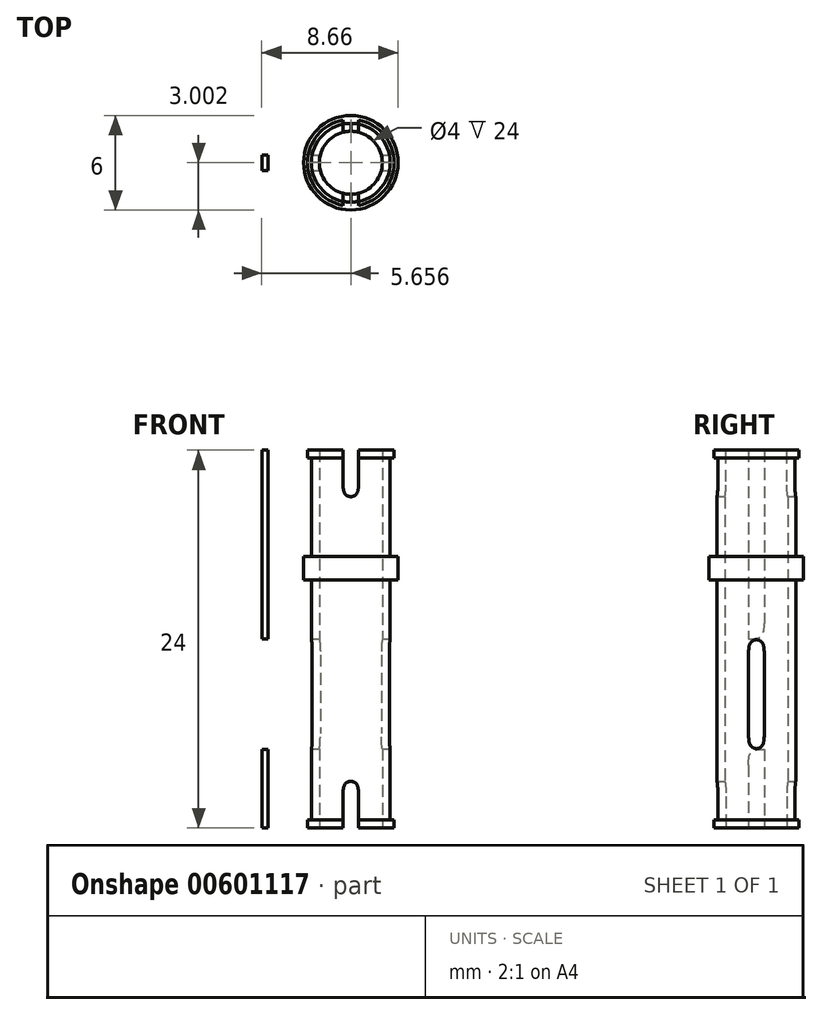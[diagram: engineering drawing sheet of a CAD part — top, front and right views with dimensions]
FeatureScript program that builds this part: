
annotation { "Feature Type Name" : "Feature", "Feature Type Description" : "" }
export const myFeature = defineFeature(function(context is Context, id is Id, definition is map)
    precondition{}
    {
        {
            var Q0;
            Q0=qCreatedBy(makeId("Top.planeOp"),FACE);
            var sketch = newSketch(context, id + "F0", { "sketchPlane" : qUnion([Q0])});
            skCircle(sketch, "E0", {"center": v(-5.92, -30) * mm, "radius": 3 * mm});
            skSolve(sketch);
        }
        {
            var Q0;
            Q0=qSketchRegion(id+"F0",true);
            extrude(context, id + "F1", {"entities" : qUnion([Q0]), "depth" : 24 * mm, "offsetDistance" : 25 * mm});
        }
        {
            var Q0;
            Q0=makeQuery(id+"F1.opExtrude","CAP_FACE",FACE,{"disambiguationData":[OSD([sQuery(id+"F0.wireOp",EDGE,"E0")])],"isStart":false});
            var sketch = newSketch(context, id + "F2", { "sketchPlane" : qUnion([Q0])});
            skCircle(sketch, "E1", {"center": v(-5.92, -30) * mm, "radius": 2.5 * mm});
            skSolve(sketch);
        }
        {
            var Q0;
            Q0=makeQuery(id+"F2.imprint","IMPRINT",FACE,{"disambiguationData":[TD([[makeQuery(id+"F2.imprint","IMPRINT",EDGE,{"derivedFrom":sQuery(id+"F2.wireOp",EDGE,"E1")}),-1.0]])]});
            extrude(context, id + "F3", {"entities" : qUnion([Q0]), "operationType" : NewBodyOperationType.REMOVE, "oppositeDirection" : true, "depth" : 6.75 * mm, "offsetDistance" : 25 * mm});
        }
        {
            var Q0;
            Q0=makeQuery(id+"F1.opExtrude","CAP_FACE",FACE,{"disambiguationData":[OSD([sQuery(id+"F0.wireOp",EDGE,"E0")])],"isStart":false});
            var sketch = newSketch(context, id + "F4", { "sketchPlane" : qUnion([Q0])});
            skCircle(sketch, "E2", {"center": v(-5.92, -30) * mm, "radius": 2.75 * mm});
            skSolve(sketch);
        }
        {
            var Q0;
            Q0=qSketchRegion(id+"F4",true);
            extrude(context, id + "F5", {"entities" : qUnion([Q0]), "operationType" : NewBodyOperationType.ADD, "oppositeDirection" : true, "depth" : .5 * mm, "offsetDistance" : 25 * mm});
        }
        {
            var Q0;
            Q0=makeQuery(id+"F1.opExtrude","CAP_FACE",FACE,{"disambiguationData":[OSD([sQuery(id+"F0.wireOp",EDGE,"E0")])],"isStart":true});
            var sketch = newSketch(context, id + "F6", { "sketchPlane" : qUnion([Q0])});
            skCircle(sketch, "E3", {"center": v(-5.92, 30) * mm, "radius": 2.5 * mm});
            skSolve(sketch);
        }
        {
            var Q0;
            Q0=makeQuery(id+"F6.imprint","IMPRINT",FACE,{"disambiguationData":[TD([[makeQuery(id+"F6.imprint","IMPRINT",EDGE,{"derivedFrom":sQuery(id+"F6.wireOp",EDGE,"E3")}),-1.0]])]});
            extrude(context, id + "F7", {"entities" : qUnion([Q0]), "operationType" : NewBodyOperationType.REMOVE, "oppositeDirection" : true, "depth" : 6.75 * mm, "offsetDistance" : 25 * mm});
        }
        {
            var Q0;
            Q0=makeQuery(id+"F1.opExtrude","CAP_FACE",FACE,{"disambiguationData":[OSD([sQuery(id+"F0.wireOp",EDGE,"E0")])],"isStart":true});
            var sketch = newSketch(context, id + "F8", { "sketchPlane" : qUnion([Q0])});
            skCircle(sketch, "E4", {"center": v(-5.92, 30) * mm, "radius": 2.75 * mm});
            skSolve(sketch);
        }
        {
            var Q0;
            Q0=qSketchRegion(id+"F8",true);
            extrude(context, id + "F9", {"entities" : qUnion([Q0]), "operationType" : NewBodyOperationType.ADD, "oppositeDirection" : true, "depth" : .5 * mm, "offsetDistance" : 25 * mm});
        }
        {
            var Q0;
            Q0=makeQuery(id+"F9.boolean.opBoolean","MERGE",FACE,{"derivedFrom":[makeQuery(id+"F1.opExtrude","CAP_FACE",FACE,{"disambiguationData":[OSD([sQuery(id+"F0.wireOp",EDGE,"E0")])],"isStart":true}),makeQuery(id+"F9.opExtrude","CAP_FACE",FACE,{"disambiguationData":[OSD([sQuery(id+"F8.wireOp",EDGE,"E4")])],"isStart":true})]});
            var sketch = newSketch(context, id + "F10", { "sketchPlane" : qUnion([Q0])});
            skCircle(sketch, "E5", {"center": v(-5.92, 30) * mm, "radius": 2 * mm});
            skSolve(sketch);
        }
        {
            var Q0;
            Q0=qSketchRegion(id+"F10",true);
            extrude(context, id + "F11", {"entities" : qUnion([Q0]), "operationType" : NewBodyOperationType.REMOVE, "oppositeDirection" : true, "depth" : 25 * mm, "offsetDistance" : 25 * mm});
        }
        {
            var Q0;
            Q0=makeQuery(id+"F5.boolean.opBoolean","MERGE",FACE,{"derivedFrom":[makeQuery(id+"F1.opExtrude","CAP_FACE",FACE,{"disambiguationData":[OSD([sQuery(id+"F0.wireOp",EDGE,"E0")])],"isStart":false}),makeQuery(id+"F5.opExtrude","CAP_FACE",FACE,{"disambiguationData":[OSD([sQuery(id+"F4.wireOp",EDGE,"E2")])],"isStart":true})]});
            var sketch = newSketch(context, id + "F12", { "sketchPlane" : qUnion([Q0])});
            skLineSegment(sketch, "E6", {"start": v(-5.92, -33.03) * mm, "end": v(-5.42, -33.03) * mm});
            skLineSegment(sketch, "E7", {"start": v(-5.42, -33.03) * mm, "end": v(-5.42, -27) * mm});
            skLineSegment(sketch, "E8", {"start": v(-5.42, -27) * mm, "end": v(-6.42, -27) * mm});
            skLineSegment(sketch, "E9", {"start": v(-6.42, -27) * mm, "end": v(-6.42, -33.03) * mm});
            skLineSegment(sketch, "E10", {"start": v(-6.42, -33.03) * mm, "end": v(-5.92, -33.03) * mm});
            skSolve(sketch);
        }
        {
            var Q0;
            {var subQ0=sQuery(id+"F12.wireOp",EDGE,"E7");var subQ1=sQuery(id+"F4.wireOp",EDGE,"E2");var subQ2=makeQuery(id+"F5.opExtrude","CAP_EDGE",EDGE,{"disambiguationData":[OSD([subQ1])],"isStart":true});var subQ3=makeQuery(id+"F12.imprint","INTERSECT",VERTEX,{"disambiguationData":[OD(0.0)],"derivedFrom":[subQ2,subQ0]});Q0=makeQuery(id+"F12.imprint","IMPRINT",FACE,{"disambiguationData":[TD([[makeQuery(id+"F12.imprint","IMPRINT",EDGE,{"disambiguationData":[TD([[subQ3,1.0]])],"derivedFrom":subQ2}),1.0]])]});}
            var Q1;
            {var subQ0=sQuery(id+"F12.wireOp",EDGE,"E7");var subQ1=sQuery(id+"F4.wireOp",EDGE,"E2");var subQ2=makeQuery(id+"F5.opExtrude","CAP_EDGE",EDGE,{"disambiguationData":[OSD([subQ1])],"isStart":true});var subQ3=makeQuery(id+"F12.imprint","INTERSECT",VERTEX,{"disambiguationData":[OD(1.0)],"derivedFrom":[subQ2,subQ0]});Q1=makeQuery(id+"F12.imprint","IMPRINT",FACE,{"disambiguationData":[TD([[makeQuery(id+"F12.imprint","IMPRINT",EDGE,{"disambiguationData":[TD([[subQ3,-1.0]])],"derivedFrom":subQ2}),1.0]])]});}
            extrude(context, id + "F13", {"entities" : qUnion([Q0, Q1]), "operationType" : NewBodyOperationType.REMOVE, "oppositeDirection" : true, "depth" : 3 * mm, "offsetDistance" : 25 * mm});
        }
        {
            var Q0;
            Q0=makeQuery(id+"F9.boolean.opBoolean","MERGE",FACE,{"derivedFrom":[makeQuery(id+"F1.opExtrude","CAP_FACE",FACE,{"disambiguationData":[OSD([sQuery(id+"F0.wireOp",EDGE,"E0")])],"isStart":true}),makeQuery(id+"F9.opExtrude","CAP_FACE",FACE,{"disambiguationData":[OSD([sQuery(id+"F8.wireOp",EDGE,"E4")])],"isStart":true})]});
            var sketch = newSketch(context, id + "F14", { "sketchPlane" : qUnion([Q0])});
            skLineSegment(sketch, "E11", {"start": v(-5.92, 33.1) * mm, "end": v(-5.42, 33.1) * mm});
            skLineSegment(sketch, "E12", {"start": v(-5.42, 33.1) * mm, "end": v(-5.42, 26.78) * mm});
            skLineSegment(sketch, "E13", {"start": v(-5.42, 26.78) * mm, "end": v(-6.42, 26.78) * mm});
            skLineSegment(sketch, "E14", {"start": v(-6.42, 26.78) * mm, "end": v(-6.42, 33.1) * mm});
            skLineSegment(sketch, "E15", {"start": v(-6.42, 33.1) * mm, "end": v(-5.92, 33.1) * mm});
            skSolve(sketch);
        }
        {
            var Q0;
            Q0=qSketchRegion(id+"F14",true);
            extrude(context, id + "F15", {"entities" : qUnion([Q0]), "operationType" : NewBodyOperationType.REMOVE, "oppositeDirection" : true, "depth" : 3 * mm, "offsetDistance" : 25 * mm});
        }
        {
            var Q0;
            Q0=makeQuery(id+"F7.boolean.opBoolean","COPY",FACE,{"derivedFrom":makeQuery(id+"F7.opExtrude","CAP_FACE",FACE,{"disambiguationData":[OSD([sQuery(id+"F0.wireOp",EDGE,"E0"),sQuery(id+"F6.wireOp",EDGE,"E3")])],"isStart":false})});
            extrude(context, id + "F16", {"entities" : qUnion([Q0]), "operationType" : NewBodyOperationType.REMOVE, "oppositeDirection" : true, "depth" : 9 * mm, "offsetDistance" : 25 * mm});
        }
        {
            var Q0;
            {var subQ0=sQuery(id+"F12.wireOp",EDGE,"E9");var subQ1=sQuery(id+"F4.wireOp",EDGE,"E2");Q0=makeQuery(id+"F13.boolean.opBoolean","COPY",EDGE,{"derivedFrom":makeQuery(id+"F13.opExtrude","CAP_EDGE",EDGE,{"disambiguationData":[OSD([subQ0]),TDD([makeQuery(id+"F12.imprint","IMPRINT",EDGE,{"disambiguationData":[TD([[makeQuery(id+"F12.imprint","INTERSECT",VERTEX,{"disambiguationData":[OD(1.0)],"derivedFrom":[makeQuery(id+"F5.opExtrude","CAP_EDGE",EDGE,{"disambiguationData":[OSD([subQ1])],"isStart":true}),subQ0]}),1.0]])],"derivedFrom":subQ0})])],"isStart":false})});}
            var Q1;
            {var subQ0=sQuery(id+"F12.wireOp",EDGE,"E7");var subQ1=sQuery(id+"F4.wireOp",EDGE,"E2");Q1=makeQuery(id+"F13.boolean.opBoolean","COPY",EDGE,{"derivedFrom":makeQuery(id+"F13.opExtrude","CAP_EDGE",EDGE,{"disambiguationData":[OSD([subQ0]),TDD([makeQuery(id+"F12.imprint","IMPRINT",EDGE,{"disambiguationData":[TD([[makeQuery(id+"F12.imprint","INTERSECT",VERTEX,{"disambiguationData":[OD(0.0)],"derivedFrom":[makeQuery(id+"F5.opExtrude","CAP_EDGE",EDGE,{"disambiguationData":[OSD([subQ1])],"isStart":true}),subQ0]}),-1.0]])],"derivedFrom":subQ0})])],"isStart":false})});}
            var Q2;
            {var subQ0=sQuery(id+"F12.wireOp",EDGE,"E7");var subQ1=sQuery(id+"F4.wireOp",EDGE,"E2");Q2=makeQuery(id+"F13.boolean.opBoolean","COPY",EDGE,{"derivedFrom":makeQuery(id+"F13.opExtrude","CAP_EDGE",EDGE,{"disambiguationData":[OSD([subQ0]),TDD([makeQuery(id+"F12.imprint","IMPRINT",EDGE,{"disambiguationData":[TD([[makeQuery(id+"F12.imprint","INTERSECT",VERTEX,{"disambiguationData":[OD(1.0)],"derivedFrom":[makeQuery(id+"F5.opExtrude","CAP_EDGE",EDGE,{"disambiguationData":[OSD([subQ1])],"isStart":true}),subQ0]}),1.0]])],"derivedFrom":subQ0})])],"isStart":false})});}
            var Q3;
            {var subQ0=sQuery(id+"F12.wireOp",EDGE,"E9");var subQ1=sQuery(id+"F4.wireOp",EDGE,"E2");Q3=makeQuery(id+"F13.boolean.opBoolean","COPY",EDGE,{"derivedFrom":makeQuery(id+"F13.opExtrude","CAP_EDGE",EDGE,{"disambiguationData":[OSD([subQ0]),TDD([makeQuery(id+"F12.imprint","IMPRINT",EDGE,{"disambiguationData":[TD([[makeQuery(id+"F12.imprint","INTERSECT",VERTEX,{"disambiguationData":[OD(0.0)],"derivedFrom":[makeQuery(id+"F5.opExtrude","CAP_EDGE",EDGE,{"disambiguationData":[OSD([subQ1])],"isStart":true}),subQ0]}),-1.0]])],"derivedFrom":subQ0})])],"isStart":false})});}
            var Q4;
            Q4=makeQuery(id+"F15.boolean.opBoolean","COPY",EDGE,{"disambiguationData":[OD(0.0)],"derivedFrom":makeQuery(id+"F15.opExtrude","CAP_EDGE",EDGE,{"disambiguationData":[OSD([sQuery(id+"F14.wireOp",EDGE,"E12")])],"isStart":false})});
            var Q5;
            Q5=makeQuery(id+"F15.boolean.opBoolean","COPY",EDGE,{"disambiguationData":[OD(0.0)],"derivedFrom":makeQuery(id+"F15.opExtrude","CAP_EDGE",EDGE,{"disambiguationData":[OSD([sQuery(id+"F14.wireOp",EDGE,"E14")])],"isStart":false})});
            var Q6;
            Q6=makeQuery(id+"F15.boolean.opBoolean","COPY",EDGE,{"disambiguationData":[OD(1.0)],"derivedFrom":makeQuery(id+"F15.opExtrude","CAP_EDGE",EDGE,{"disambiguationData":[OSD([sQuery(id+"F14.wireOp",EDGE,"E12")])],"isStart":false})});
            var Q7;
            Q7=makeQuery(id+"F15.boolean.opBoolean","COPY",EDGE,{"disambiguationData":[OD(1.0)],"derivedFrom":makeQuery(id+"F15.opExtrude","CAP_EDGE",EDGE,{"disambiguationData":[OSD([sQuery(id+"F14.wireOp",EDGE,"E14")])],"isStart":false})});
            fillet(context, id + "F17", {"entities" : qUnion([Q0, Q1, Q2, Q3, Q4, Q5, Q6, Q7]), "radius" : 1 * mm, "tangentPropagation" : true, "rho" : .65, "crossSection" : FilletCrossSection.CONIC, "allowEdgeOverflow" : false});
        }
        {
            var Q0;
            {var subQ0=sQuery(id+"F8.wireOp",EDGE,"E4");Q0=makeQuery(id+"F15.boolean.opBoolean","SPLIT",FACE,{"disambiguationData":[TD([makeQuery(id+"F15.opExtrude","SWEPT_FACE",FACE,{"disambiguationData":[OSD([sQuery(id+"F14.wireOp",EDGE,"E14")])]})])],"derivedFrom":makeQuery(id+"F9.boolean.opBoolean","MERGE",FACE,{"derivedFrom":[makeQuery(id+"F1.opExtrude","CAP_FACE",FACE,{"disambiguationData":[OSD([sQuery(id+"F0.wireOp",EDGE,"E0")])],"isStart":true}),makeQuery(id+"F9.opExtrude","CAP_FACE",FACE,{"disambiguationData":[OSD([subQ0])],"isStart":true})]})});}
            var sketch = newSketch(context, id + "F18", { "sketchPlane" : qUnion([Q0])});
            skPoint(sketch, "E16.endSnap0", {"position": v(-8.67, 30) * mm});
            skLineSegment(sketch, "E17", {"start": v(-11.58, 30) * mm, "end": v(-11.58, 29.5) * mm});
            skLineSegment(sketch, "E18", {"start": v(-11.58, 29.5) * mm, "end": v(-11.18, 29.5) * mm});
            skLineSegment(sketch, "E19", {"start": v(-11.18, 29.5) * mm, "end": v(-11.18, 30.5) * mm});
            skLineSegment(sketch, "E20", {"start": v(-11.18, 30.5) * mm, "end": v(-11.58, 30.5) * mm});
            skLineSegment(sketch, "E21", {"start": v(-11.58, 30.5) * mm, "end": v(-11.58, 30) * mm});
            skSolve(sketch);
        }
        {
            var Q0;
            Q0=makeQuery(id+"F18.imprint","IMPRINT",FACE,{"disambiguationData":[TD([[makeQuery(id+"F18.imprint","IMPRINT",EDGE,{"derivedFrom":sQuery(id+"F18.wireOp",EDGE,"E17")}),1.0]])]});
            extrude(context, id + "F19", {"entities" : qUnion([Q0]), "oppositeDirection" : true, "depth" : 24 * mm, "offsetDistance" : 25 * mm});
        }
        {
            var Q0;
            Q0=makeQuery(id+"F19.opExtrude","SWEPT_FACE",FACE,{"disambiguationData":[OSD([sQuery(id+"F18.wireOp",EDGE,"E17"),sQuery(id+"F18.wireOp",EDGE,"E21")])]});
            var sketch = newSketch(context, id + "F20", { "sketchPlane" : qUnion([Q0])});
            skLineSegment(sketch, "E22", {"start": v(29.5, 24) * mm, "end": v(29.5, 16.5) * mm});
            skLineSegment(sketch, "E23", {"start": v(29.5, 16.5) * mm, "end": v(29.5, 20) * mm});
            skLineSegment(sketch, "E24", {"start": v(29.5, 20) * mm, "end": v(30.5, 20) * mm});
            skLineSegment(sketch, "E25", {"start": v(30.5, 20) * mm, "end": v(30.5, 13) * mm});
            skLineSegment(sketch, "E26", {"start": v(30.5, 13) * mm, "end": v(29.5, 13) * mm});
            skLineSegment(sketch, "E27", {"start": v(29.5, 13) * mm, "end": v(29.5, 16.5) * mm});
            skLineSegment(sketch, "E28", {"start": v(29.5, 13) * mm, "end": v(29.5, 12) * mm});
            skLineSegment(sketch, "E29", {"start": v(29.5, 12) * mm, "end": v(29.5, 5) * mm});
            skLineSegment(sketch, "E30", {"start": v(29.5, 5) * mm, "end": v(30.5, 5) * mm});
            skLineSegment(sketch, "E31", {"start": v(30.5, 5) * mm, "end": v(30.5, 12) * mm});
            skLineSegment(sketch, "E32", {"start": v(30.5, 12) * mm, "end": v(29.5, 12) * mm});
            skSolve(sketch);
        }
        {
            var Q0;
            Q0=makeQuery(id+"F20.imprint","IMPRINT",FACE,{"disambiguationData":[TD([[makeQuery(id+"F20.imprint","IMPRINT",EDGE,{"derivedFrom":sQuery(id+"F20.wireOp",EDGE,"E23")}),1.0]])]});
            var Q1;
            Q1=makeQuery(id+"F20.imprint","IMPRINT",FACE,{"disambiguationData":[TD([[makeQuery(id+"F20.imprint","IMPRINT",EDGE,{"derivedFrom":sQuery(id+"F20.wireOp",EDGE,"E29")}),1.0]])]});
            extrude(context, id + "F21", {"entities" : qUnion([Q0, Q1]), "operationType" : NewBodyOperationType.REMOVE, "oppositeDirection" : true, "depth" : 25 * mm, "offsetDistance" : 25 * mm});
        }
        {
            var Q0;
            Q0=makeQuery(id+"F21.boolean.opBoolean","COPY",EDGE,{"disambiguationData":[OD(1.0)],"derivedFrom":makeQuery(id+"F21.opExtrude","SWEPT_EDGE",EDGE,{"disambiguationData":[OSD([sQuery(id+"F18.wireOp",EDGE,"E20"),sQuery(id+"F18.wireOp",EDGE,"E21"),sQuery(id+"F20.wireOp",EDGE,"E30"),sQuery(id+"F20.wireOp",EDGE,"E31")])]})});
            var Q1;
            Q1=makeQuery(id+"F21.boolean.opBoolean","COPY",EDGE,{"disambiguationData":[OD(1.0)],"derivedFrom":makeQuery(id+"F21.opExtrude","SWEPT_EDGE",EDGE,{"disambiguationData":[OSD([sQuery(id+"F18.wireOp",EDGE,"E17"),sQuery(id+"F18.wireOp",EDGE,"E18"),sQuery(id+"F20.wireOp",EDGE,"E29"),sQuery(id+"F20.wireOp",EDGE,"E30")])]})});
            var Q2;
            Q2=makeQuery(id+"F21.boolean.opBoolean","COPY",EDGE,{"disambiguationData":[OD(1.0)],"derivedFrom":makeQuery(id+"F21.opExtrude","SWEPT_EDGE",EDGE,{"disambiguationData":[OSD([sQuery(id+"F18.wireOp",EDGE,"E20"),sQuery(id+"F18.wireOp",EDGE,"E21"),sQuery(id+"F20.wireOp",EDGE,"E31"),sQuery(id+"F20.wireOp",EDGE,"E32")])]})});
            var Q3;
            Q3=makeQuery(id+"F21.boolean.opBoolean","COPY",EDGE,{"disambiguationData":[OD(1.0)],"derivedFrom":makeQuery(id+"F21.opExtrude","SWEPT_EDGE",EDGE,{"disambiguationData":[OSD([sQuery(id+"F20.wireOp",EDGE,"E28"),sQuery(id+"F20.wireOp",EDGE,"E29"),sQuery(id+"F20.wireOp",EDGE,"E32")])]})});
            var Q4;
            Q4=makeQuery(id+"F21.boolean.opBoolean","COPY",EDGE,{"disambiguationData":[OD(1.0)],"derivedFrom":makeQuery(id+"F21.opExtrude","SWEPT_EDGE",EDGE,{"disambiguationData":[OSD([sQuery(id+"F20.wireOp",EDGE,"E26"),sQuery(id+"F20.wireOp",EDGE,"E27"),sQuery(id+"F20.wireOp",EDGE,"E28")])]})});
            var Q5;
            Q5=makeQuery(id+"F21.boolean.opBoolean","COPY",EDGE,{"disambiguationData":[OD(1.0)],"derivedFrom":makeQuery(id+"F21.opExtrude","SWEPT_EDGE",EDGE,{"disambiguationData":[OSD([sQuery(id+"F18.wireOp",EDGE,"E20"),sQuery(id+"F18.wireOp",EDGE,"E21"),sQuery(id+"F20.wireOp",EDGE,"E25"),sQuery(id+"F20.wireOp",EDGE,"E26")])]})});
            var Q6;
            Q6=makeQuery(id+"F21.boolean.opBoolean","COPY",EDGE,{"disambiguationData":[OD(1.0)],"derivedFrom":makeQuery(id+"F21.opExtrude","SWEPT_EDGE",EDGE,{"disambiguationData":[OSD([sQuery(id+"F18.wireOp",EDGE,"E20"),sQuery(id+"F18.wireOp",EDGE,"E21"),sQuery(id+"F20.wireOp",EDGE,"E24"),sQuery(id+"F20.wireOp",EDGE,"E25")])]})});
            var Q7;
            Q7=makeQuery(id+"F21.boolean.opBoolean","COPY",EDGE,{"disambiguationData":[OD(1.0)],"derivedFrom":makeQuery(id+"F21.opExtrude","SWEPT_EDGE",EDGE,{"disambiguationData":[OSD([sQuery(id+"F20.wireOp",EDGE,"E22"),sQuery(id+"F20.wireOp",EDGE,"E23"),sQuery(id+"F20.wireOp",EDGE,"E24")])]})});
            var Q8;
            Q8=makeQuery(id+"F21.boolean.opBoolean","COPY",EDGE,{"disambiguationData":[OD(0.0)],"derivedFrom":makeQuery(id+"F21.opExtrude","SWEPT_EDGE",EDGE,{"disambiguationData":[OSD([sQuery(id+"F20.wireOp",EDGE,"E22"),sQuery(id+"F20.wireOp",EDGE,"E23"),sQuery(id+"F20.wireOp",EDGE,"E24")])]})});
            var Q9;
            Q9=makeQuery(id+"F21.boolean.opBoolean","COPY",EDGE,{"disambiguationData":[OD(0.0)],"derivedFrom":makeQuery(id+"F21.opExtrude","SWEPT_EDGE",EDGE,{"disambiguationData":[OSD([sQuery(id+"F18.wireOp",EDGE,"E20"),sQuery(id+"F18.wireOp",EDGE,"E21"),sQuery(id+"F20.wireOp",EDGE,"E24"),sQuery(id+"F20.wireOp",EDGE,"E25")])]})});
            var Q10;
            Q10=makeQuery(id+"F21.boolean.opBoolean","COPY",EDGE,{"disambiguationData":[OD(0.0)],"derivedFrom":makeQuery(id+"F21.opExtrude","SWEPT_EDGE",EDGE,{"disambiguationData":[OSD([sQuery(id+"F18.wireOp",EDGE,"E20"),sQuery(id+"F18.wireOp",EDGE,"E21"),sQuery(id+"F20.wireOp",EDGE,"E25"),sQuery(id+"F20.wireOp",EDGE,"E26")])]})});
            var Q11;
            Q11=makeQuery(id+"F21.boolean.opBoolean","COPY",EDGE,{"disambiguationData":[OD(0.0)],"derivedFrom":makeQuery(id+"F21.opExtrude","SWEPT_EDGE",EDGE,{"disambiguationData":[OSD([sQuery(id+"F20.wireOp",EDGE,"E26"),sQuery(id+"F20.wireOp",EDGE,"E27"),sQuery(id+"F20.wireOp",EDGE,"E28")])]})});
            var Q12;
            Q12=makeQuery(id+"F21.boolean.opBoolean","COPY",EDGE,{"disambiguationData":[OD(0.0)],"derivedFrom":makeQuery(id+"F21.opExtrude","SWEPT_EDGE",EDGE,{"disambiguationData":[OSD([sQuery(id+"F18.wireOp",EDGE,"E17"),sQuery(id+"F18.wireOp",EDGE,"E18"),sQuery(id+"F20.wireOp",EDGE,"E29"),sQuery(id+"F20.wireOp",EDGE,"E30")])]})});
            var Q13;
            Q13=makeQuery(id+"F21.boolean.opBoolean","COPY",EDGE,{"disambiguationData":[OD(0.0)],"derivedFrom":makeQuery(id+"F21.opExtrude","SWEPT_EDGE",EDGE,{"disambiguationData":[OSD([sQuery(id+"F18.wireOp",EDGE,"E20"),sQuery(id+"F18.wireOp",EDGE,"E21"),sQuery(id+"F20.wireOp",EDGE,"E30"),sQuery(id+"F20.wireOp",EDGE,"E31")])]})});
            var Q14;
            Q14=makeQuery(id+"F21.boolean.opBoolean","COPY",EDGE,{"disambiguationData":[OD(0.0)],"derivedFrom":makeQuery(id+"F21.opExtrude","SWEPT_EDGE",EDGE,{"disambiguationData":[OSD([sQuery(id+"F20.wireOp",EDGE,"E28"),sQuery(id+"F20.wireOp",EDGE,"E29"),sQuery(id+"F20.wireOp",EDGE,"E32")])]})});
            var Q15;
            Q15=makeQuery(id+"F21.boolean.opBoolean","COPY",EDGE,{"disambiguationData":[OD(0.0)],"derivedFrom":makeQuery(id+"F21.opExtrude","SWEPT_EDGE",EDGE,{"disambiguationData":[OSD([sQuery(id+"F18.wireOp",EDGE,"E20"),sQuery(id+"F18.wireOp",EDGE,"E21"),sQuery(id+"F20.wireOp",EDGE,"E31"),sQuery(id+"F20.wireOp",EDGE,"E32")])]})});
            fillet(context, id + "F22", {"entities" : qUnion([Q0, Q1, Q2, Q3, Q4, Q5, Q6, Q7, Q8, Q9, Q10, Q11, Q12, Q13, Q14, Q15]), "radius" : 1 * mm, "tangentPropagation" : true, "rho" : .65, "crossSection" : FilletCrossSection.CONIC, "allowEdgeOverflow" : false});
        }
    });
